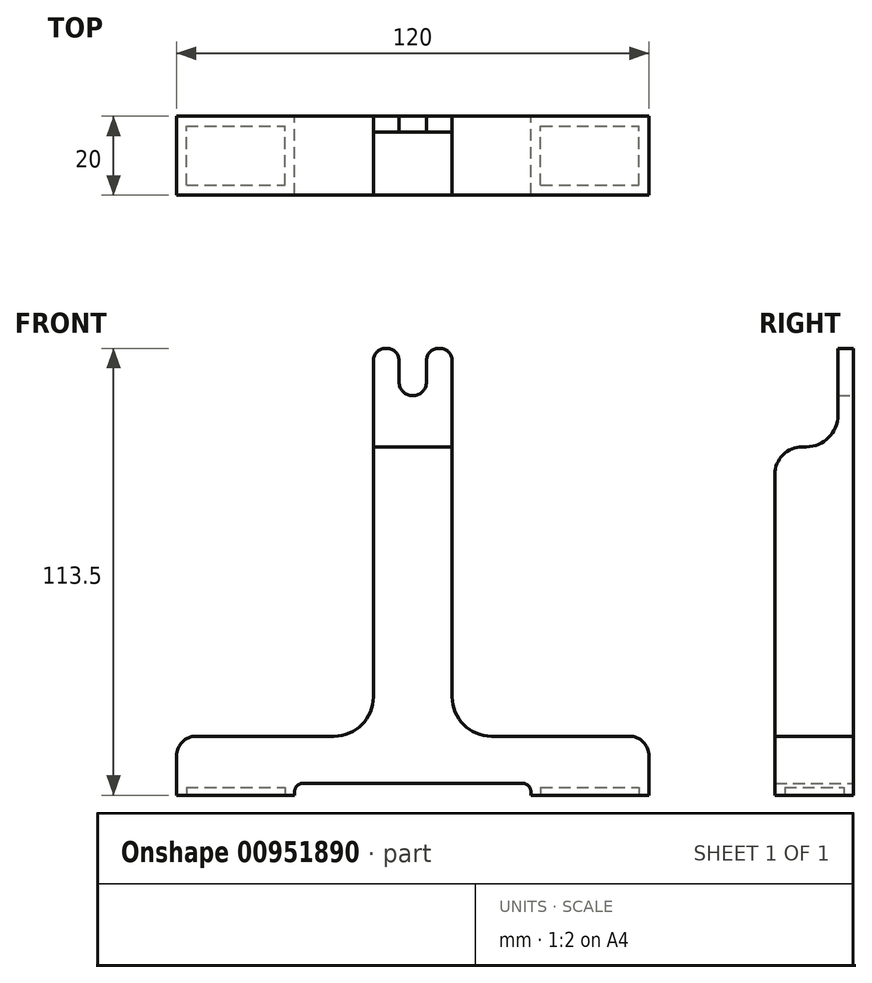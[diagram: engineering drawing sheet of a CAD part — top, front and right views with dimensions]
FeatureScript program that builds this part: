
annotation { "Feature Type Name" : "Feature", "Feature Type Description" : "" }
export const myFeature = defineFeature(function(context is Context, id is Id, definition is map)
    precondition{}
    {
        {
            var Q0;
            Q0=qCreatedBy(makeId("Front.planeOp"),FACE);
            var sketch = newSketch(context, id + "F0", { "sketchPlane" : qUnion([Q0])});
            skArc(sketch, "E0", {"start": v(-3.5, 105) * mm, "mid": v(0, 101.5) * mm, "end": v(3.5, 105) * mm});
            skCircle(sketch, "E1", {"center": v(0, 105) * mm, "radius": 100 * mm, "construction": true});
            skLineSegment(sketch, "E2", {"start": v(-10, 110.5) * mm, "end": v(-10, 25) * mm});
            skLineSegment(sketch, "E3", {"start": v(-20, 15) * mm, "end": v(-55, 15) * mm});
            skLineSegment(sketch, "E4", {"start": v(-60, 10) * mm, "end": v(-60, 0) * mm});
            skLineSegment(sketch, "E5", {"start": v(-60, 0) * mm, "end": v(-30, 0) * mm});
            skLineSegment(sketch, "E6", {"start": v(-28, 3) * mm, "end": v(28, 3) * mm});
            skLineSegment(sketch, "E7", {"start": v(30, 0) * mm, "end": v(60, 0) * mm});
            skLineSegment(sketch, "E8", {"start": v(60, 0) * mm, "end": v(60, 10) * mm});
            skLineSegment(sketch, "E9", {"start": v(55, 15) * mm, "end": v(20, 15) * mm});
            skLineSegment(sketch, "E10", {"start": v(10, 25) * mm, "end": v(10, 110.5) * mm});
            skLineSegment(sketch, "E11", {"start": v(7, 113.5) * mm, "end": v(6.5, 113.5) * mm});
            skLineSegment(sketch, "E12", {"start": v(-30, 1) * mm, "end": v(-30, 0) * mm});
            skLineSegment(sketch, "E13", {"start": v(30, 1) * mm, "end": v(30, 0) * mm});
            skPoint(sketch, "E14.orphan", {"position": v(-45, 0) * mm});
            skPoint(sketch, "E15.orphan", {"position": v(45, 0) * mm});
            skPoint(sketch, "E16.visualSharp", {"position": v(-10, 15) * mm});
            skArc(sketch, "E16.filletArc", {"start": v(-20, 15) * mm, "mid": v(-12.93, 17.93) * mm, "end": v(-10, 25) * mm});
            skPoint(sketch, "E17.visualSharp", {"position": v(10, 15) * mm});
            skArc(sketch, "E17.filletArc", {"start": v(10, 25) * mm, "mid": v(12.93, 17.93) * mm, "end": v(20, 15) * mm});
            skPoint(sketch, "E18.visualSharp", {"position": v(-10, 113.5) * mm});
            skArc(sketch, "E18.filletArc", {"start": v(-7, 113.5) * mm, "mid": v(-9.12, 112.62) * mm, "end": v(-10, 110.5) * mm});
            skPoint(sketch, "E19.visualSharp", {"position": v(10, 113.5) * mm});
            skArc(sketch, "E19.filletArc", {"start": v(10, 110.5) * mm, "mid": v(9.12, 112.62) * mm, "end": v(7, 113.5) * mm});
            skPoint(sketch, "E20.visualSharp", {"position": v(-60, 15) * mm});
            skArc(sketch, "E20.filletArc", {"start": v(-55, 15) * mm, "mid": v(-58.54, 13.54) * mm, "end": v(-60, 10) * mm});
            skPoint(sketch, "E21.visualSharp", {"position": v(60, 15) * mm});
            skArc(sketch, "E21.filletArc", {"start": v(60, 10) * mm, "mid": v(58.54, 13.54) * mm, "end": v(55, 15) * mm});
            skPoint(sketch, "E22.visualSharp", {"position": v(30, 3) * mm});
            skArc(sketch, "E22.filletArc", {"start": v(30, 1) * mm, "mid": v(29.41, 2.41) * mm, "end": v(28, 3) * mm});
            skPoint(sketch, "E23.visualSharp", {"position": v(-30, 3) * mm});
            skArc(sketch, "E23.filletArc", {"start": v(-28, 3) * mm, "mid": v(-29.41, 2.41) * mm, "end": v(-30, 1) * mm});
            skLineSegment(sketch, "E24", {"start": v(-3.5, 105) * mm, "end": v(-3.5, 110.5) * mm});
            skLineSegment(sketch, "E25", {"start": v(3.5, 105) * mm, "end": v(3.5, 110.5) * mm});
            skLineSegment(sketch, "E26.trimOffspring", {"start": v(-6.5, 113.5) * mm, "end": v(-7, 113.5) * mm});
            skPoint(sketch, "E27.visualSharp", {"position": v(-3.5, 113.5) * mm});
            skArc(sketch, "E27.filletArc", {"start": v(-3.5, 110.5) * mm, "mid": v(-4.38, 112.62) * mm, "end": v(-6.5, 113.5) * mm});
            skPoint(sketch, "E28.visualSharp", {"position": v(3.5, 113.5) * mm});
            skArc(sketch, "E28.filletArc", {"start": v(6.5, 113.5) * mm, "mid": v(4.38, 112.62) * mm, "end": v(3.5, 110.5) * mm});
            skSolve(sketch);
        }
        {
            var Q0;
            Q0=makeQuery(id+"F0.imprint","IMPRINT",FACE,{"disambiguationData":[TD([[makeQuery(id+"F0.imprint","IMPRINT",EDGE,{"derivedFrom":sQuery(id+"F0.wireOp",EDGE,"E0")}),-1.0]])]});
            extrude(context, id + "F1", {"entities" : qUnion([Q0]), "depth" : 20 * mm, "offsetDistance" : 25 * mm});
        }
        {
            var Q0;
            Q0=makeQuery(id+"F1.opExtrude","SWEPT_FACE",FACE,{"disambiguationData":[OSD([sQuery(id+"F0.wireOp",EDGE,"E10")])]});
            var sketch = newSketch(context, id + "F2", { "sketchPlane" : qUnion([Q0])});
            skLineSegment(sketch, "E29", {"start": v(-4, 116.6) * mm, "end": v(-4, 96.5) * mm});
            skLineSegment(sketch, "E30", {"start": v(-12, 88.5) * mm, "end": v(-13, 88.5) * mm});
            skLineSegment(sketch, "E31", {"start": v(-20, 116.6) * mm, "end": v(-4, 116.6) * mm});
            skPoint(sketch, "E32.visualSharp", {"position": v(-4, 88.5) * mm});
            skArc(sketch, "E32.filletArc", {"start": v(-12, 88.5) * mm, "mid": v(-6.34, 90.84) * mm, "end": v(-4, 96.5) * mm});
            skLineSegment(sketch, "E33", {"start": v(-20, 81.5) * mm, "end": v(-20, 79.44) * mm});
            skLineSegment(sketch, "E34", {"start": v(-20, 79.44) * mm, "end": v(-25.17, 79.44) * mm});
            skLineSegment(sketch, "E35", {"start": v(-25.17, 79.44) * mm, "end": v(-25.17, 116.6) * mm});
            skLineSegment(sketch, "E36", {"start": v(-25.17, 116.6) * mm, "end": v(-20, 116.6) * mm});
            skPoint(sketch, "E37.visualSharp", {"position": v(-20, 88.5) * mm});
            skArc(sketch, "E37.filletArc", {"start": v(-13, 88.5) * mm, "mid": v(-17.95, 86.45) * mm, "end": v(-20, 81.5) * mm});
            skSolve(sketch);
        }
        {
            var Q0;
            {var subQ0=sQuery(id+"F2.wireOp",EDGE,"E31");Q0=makeQuery(id+"F2.imprint","IMPRINT",FACE,{"disambiguationData":[TD([[makeQuery(id+"F2.imprint","IMPRINT",EDGE,{"derivedFrom":subQ0}),-1.0]])]});}
            var Q1;
            Q1=makeQuery(id+"F2.imprint","IMPRINT",FACE,{"disambiguationData":[TD([[makeQuery(id+"F2.imprint","IMPRINT",EDGE,{"derivedFrom":sQuery(id+"F2.wireOp",EDGE,"E30")}),-1.0]])]});
            extrude(context, id + "F3", {"entities" : qUnion([Q0, Q1]), "operationType" : NewBodyOperationType.REMOVE, "oppositeDirection" : true, "depth" : 25 * mm, "offsetDistance" : 25 * mm});
        }
        {
            var Q0;
            Q0=makeQuery(id+"F1.opExtrude","SWEPT_FACE",FACE,{"disambiguationData":[OSD([sQuery(id+"F0.wireOp",EDGE,"E5")])]});
            var sketch = newSketch(context, id + "F4", { "sketchPlane" : qUnion([Q0])});
            skLineSegment(sketch, "E38.bottom", {"start": v(-57.5, 17.5) * mm, "end": v(-32.5, 17.5) * mm});
            skLineSegment(sketch, "E38.top", {"start": v(-57.5, 2.5) * mm, "end": v(-32.5, 2.5) * mm});
            skLineSegment(sketch, "E38.left", {"start": v(-57.5, 17.5) * mm, "end": v(-57.5, 2.5) * mm});
            skLineSegment(sketch, "E38.right", {"start": v(-32.5, 17.5) * mm, "end": v(-32.5, 2.5) * mm});
            skLineSegment(sketch, "E39.bottom", {"start": v(32.5, 17.5) * mm, "end": v(57.5, 17.5) * mm});
            skLineSegment(sketch, "E39.top", {"start": v(32.5, 2.5) * mm, "end": v(57.5, 2.5) * mm});
            skLineSegment(sketch, "E39.left", {"start": v(32.5, 17.5) * mm, "end": v(32.5, 2.5) * mm});
            skLineSegment(sketch, "E39.right", {"start": v(57.5, 17.5) * mm, "end": v(57.5, 2.5) * mm});
            skSolve(sketch);
        }
        {
            var Q0;
            Q0=makeQuery(id+"F4.imprint","IMPRINT",FACE,{"disambiguationData":[TD([[makeQuery(id+"F4.imprint","IMPRINT",EDGE,{"derivedFrom":sQuery(id+"F4.wireOp",EDGE,"E38.bottom")}),-1.0]])]});
            var Q1;
            Q1=makeQuery(id+"F4.imprint","IMPRINT",FACE,{"disambiguationData":[TD([[makeQuery(id+"F4.imprint","IMPRINT",EDGE,{"derivedFrom":sQuery(id+"F4.wireOp",EDGE,"E39.bottom")}),-1.0]])]});
            extrude(context, id + "F5", {"entities" : qUnion([Q0, Q1]), "operationType" : NewBodyOperationType.REMOVE, "oppositeDirection" : true, "depth" : 2 * mm, "offsetDistance" : 25 * mm});
        }
    });
